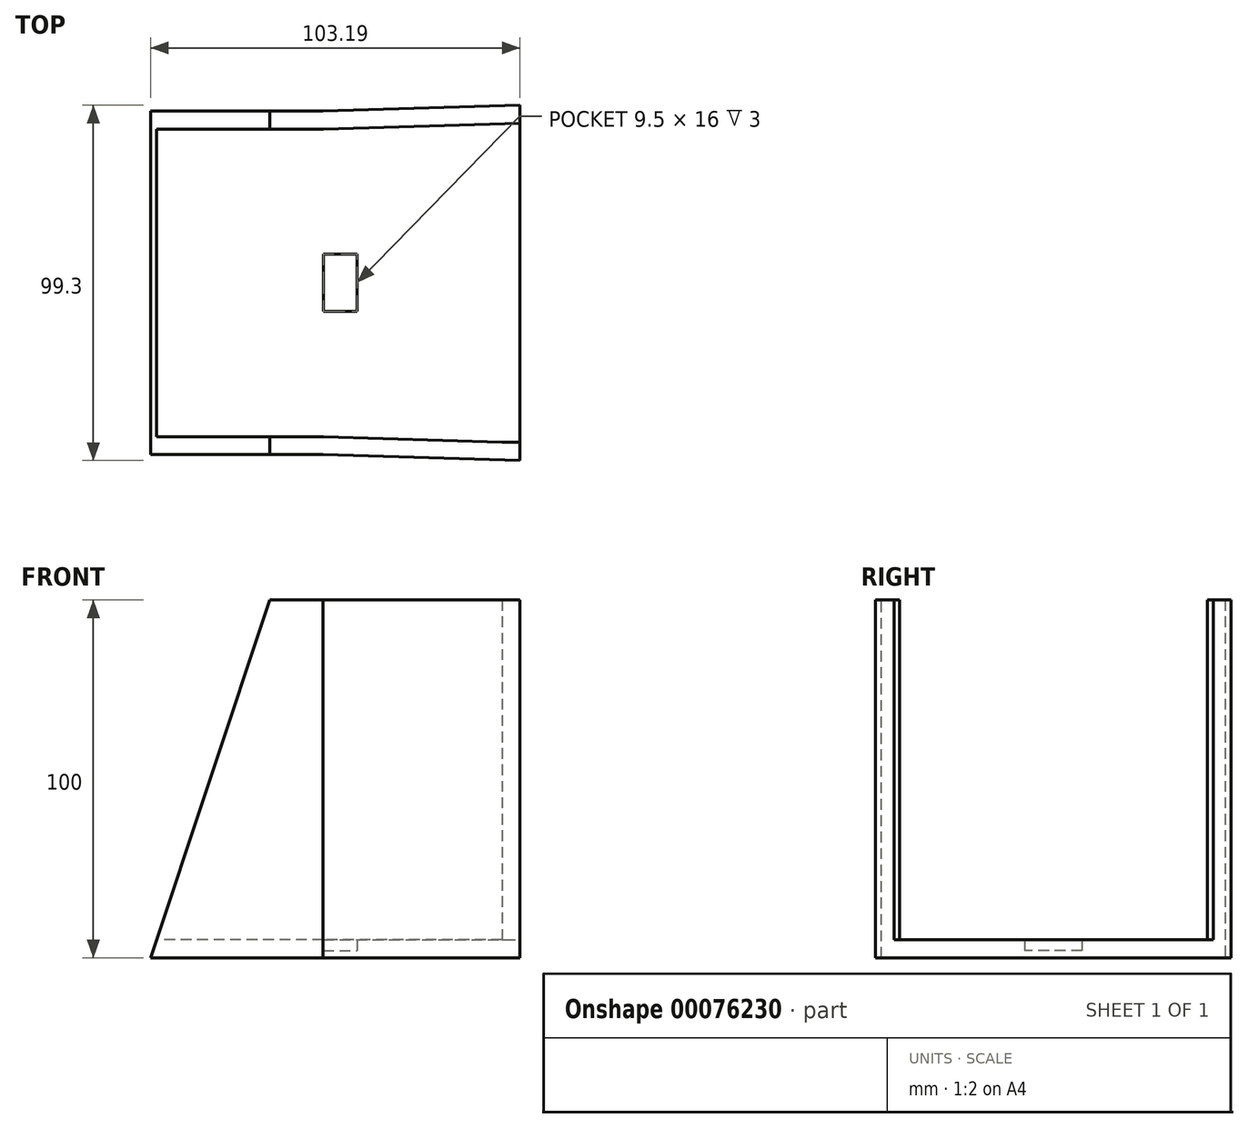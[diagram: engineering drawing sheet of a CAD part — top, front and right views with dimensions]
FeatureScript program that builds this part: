
annotation { "Feature Type Name" : "Feature", "Feature Type Description" : "" }
export const myFeature = defineFeature(function(context is Context, id is Id, definition is map)
    precondition{}
    {
        {
            var Q0;
            Q0=qCreatedBy(makeId("Top.planeOp"),FACE);
            var sketch = newSketch(context, id + "F0", { "sketchPlane" : qUnion([Q0])});
            skLineSegment(sketch, "E0", {"start": v(0, 43) * mm, "end": v(49.98, 44.5) * mm});
            skLineSegment(sketch, "E1", {"start": v(49.98, -44.5) * mm, "end": v(0, -43) * mm});
            skLineSegment(sketch, "E2.bottom", {"start": v(0, 43) * mm, "end": v(-50, 43) * mm});
            skLineSegment(sketch, "E2.top", {"start": v(0, -43) * mm, "end": v(-50, -43) * mm});
            skLineSegment(sketch, "E2.right", {"start": v(-50, 43) * mm, "end": v(-50, -43) * mm});
            skLineSegment(sketch, "E3.0", {"start": v(-0.08, 48) * mm, "end": v(54.98, 49.65) * mm});
            skLineSegment(sketch, "E3.2", {"start": v(-55, 48) * mm, "end": v(-55, -48) * mm});
            skLineSegment(sketch, "E3.3", {"start": v(-0.08, -48) * mm, "end": v(-55, -48) * mm});
            skLineSegment(sketch, "E3.4", {"start": v(54.98, -49.65) * mm, "end": v(-0.08, -48) * mm});
            skLineSegment(sketch, "E3.5", {"start": v(-0.08, 48) * mm, "end": v(-55, 48) * mm});
            skLineSegment(sketch, "E4.top", {"start": v(0, 8) * mm, "end": v(9.5, 8) * mm});
            skLineSegment(sketch, "E4.right", {"start": v(9.5, 0) * mm, "end": v(9.5, 8) * mm});
            skLineSegment(sketch, "E5.MirrorCS", {"start": v(0, -8) * mm, "end": v(9.5, -8) * mm});
            skLineSegment(sketch, "E6.MirrorCS", {"start": v(9.5, 0) * mm, "end": v(9.5, -8) * mm});
            skLineSegment(sketch, "E7", {"start": v(0, 8) * mm, "end": v(0, -8) * mm});
            skLineSegment(sketch, "E8", {"start": v(49.98, -44.5) * mm, "end": v(54.98, -44.5) * mm});
            skLineSegment(sketch, "E9", {"start": v(49.98, 44.5) * mm, "end": v(54.98, 44.65) * mm});
            skLineSegment(sketch, "E10", {"start": v(54.98, 44.65) * mm, "end": v(54.98, -44.5) * mm});
            skLineSegment(sketch, "E11", {"start": v(54.98, 44.65) * mm, "end": v(54.98, 49.65) * mm});
            skLineSegment(sketch, "E12", {"start": v(54.98, -44.5) * mm, "end": v(54.98, -49.65) * mm});
            skSolve(sketch);
        }
        {
            var Q0;
            Q0=makeQuery(id+"F0.imprint","IMPRINT",FACE,{"disambiguationData":[TD([[makeQuery(id+"F0.imprint","IMPRINT",EDGE,{"derivedFrom":sQuery(id+"F0.wireOp",EDGE,"E0")}),-1.0]])]});
            extrude(context, id + "F1", {"entities" : qUnion([Q0]), "depth" : 5 * mm});
        }
        {
            var Q0;
            Q0=makeQuery(id+"F0.imprint","IMPRINT",FACE,{"disambiguationData":[TD([[makeQuery(id+"F0.imprint","IMPRINT",EDGE,{"derivedFrom":sQuery(id+"F0.wireOp",EDGE,"E0")}),1.0]])]});
            extrude(context, id + "F2", {"entities" : qUnion([Q0]), "operationType" : NewBodyOperationType.ADD, "depth" : 100 * mm});
        }
        {
            var Q0;
            Q0=makeQuery(id+"F0.imprint","IMPRINT",FACE,{"disambiguationData":[TD([[makeQuery(id+"F0.imprint","IMPRINT",EDGE,{"derivedFrom":sQuery(id+"F0.wireOp",EDGE,"E4.top")}),-1.0]])]});
            extrude(context, id + "F3", {"entities" : qUnion([Q0]), "operationType" : NewBodyOperationType.ADD, "depth" : 2 * mm});
        }
        {
            var Q0;
            Q0=makeQuery(id+"F2.opExtrude","SWEPT_FACE",FACE,{"disambiguationData":[OSD([sQuery(id+"F0.wireOp",EDGE,"E3.3")])]});
            var sketch = newSketch(context, id + "F4", { "sketchPlane" : qUnion([Q0])});
            skLineSegment(sketch, "E13", {"start": v(-48.2, 0) * mm, "end": v(-14.94, 100) * mm});
            skSolve(sketch);
        }
        {
            var Q0;
            {var subQ0=sQuery(id+"F4.wireOp",EDGE,"E13");Q0=makeQuery(id+"F4.imprint","IMPRINT",FACE,{"disambiguationData":[TD([[makeQuery(id+"F4.imprint","IMPRINT",EDGE,{"derivedFrom":subQ0}),1.0]])]});}
            extrude(context, id + "F5", {"entities" : qUnion([Q0]), "operationType" : NewBodyOperationType.REMOVE, "oppositeDirection" : true, "depth" : 96 * mm});
        }
    });
